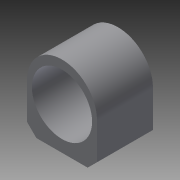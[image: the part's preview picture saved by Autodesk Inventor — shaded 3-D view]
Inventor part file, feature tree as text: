
AUTODESK INVENTOR PART (.ipt)
format: ipt  version: 2014 SP1 (Build 180222100, 222)  size: 93,696 bytes
history: native  units: mm
features: chamfer x2, extrude x1, sketch x1
ambient origin geometry x8: Origin, YZ Plane, XZ Plane, XY Plane, X Axis, Y Axis, Z Axis, Center Point
bodies: Solid1 (feature_tree)
feature tree (4):
  extrude  "Extrusion1"  Depth=7.5mm
  chamfer  "Chamfer1"  Distance=12.0mm
  chamfer  "Chamfer2"  Distance=9.0mm
  sketch  "Sketch1"  dims[d0=12.9mm d2=7.5mm d4=12.0mm d5=0.0mm d7=9.0mm d8=2.0mm d9=2.0mm d10=45.0deg d11=2.0mm d12=2.0mm d13=45.0deg]
